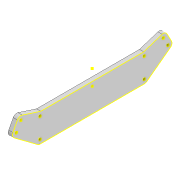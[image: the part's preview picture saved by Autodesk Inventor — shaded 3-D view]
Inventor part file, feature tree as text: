
AUTODESK INVENTOR PART (.ipt)
format: ipt  version: 2022 (Build 260153000, 153)  size: 279,040 bytes
history: native  units: mm
features: sketch x2, extrude x1, projected_geometry x1
ambient origin geometry x8: Origin, YZ Plane, XZ Plane, XY Plane, X Axis, Y Axis, Z Axis, Center Point
bodies: Solid1 (feature_tree)
feature tree (4):
  extrude  "Extrusion1"  Depth=3.9mm
  sketch  "Sketch8"  dims[d6=5.0mm d7=0.0mm d25=3.0mm d28=3.0mm d43=59.0mm d44=65.0mm d45=65.0mm d47=59.0mm d48=10.0mm d49=10.0mm d50=10.0mm d53=3.0mm d54=3.0mm d55=4.0mm d56=4.0mm d57=25.0mm d58=25.0mm d59=10.0mm d60=10.0mm d61=10.0mm d62=3.0mm d63=3.0mm d64=3.0mm d65=3.0mm d66=3.0mm d67=10.0mm d68=25.0mm d69=3.0mm d70=3.0mm d71=10.0mm d72=25.0mm d73=25.0mm d74=25.0mm d76=3.0mm d78=3.0mm d79=3.0mm d80=3.0mm d81=6.0mm d82=6.0mm d83=19.0mm d84=8.0mm d85=8.0mm d86=8.0mm d87=8.0mm d88=2.0mm d89=10.0mm d90=10.0mm d91=30.0mm d92=30.0mm]
  sketch  "Sketch1"  dims[d2=3.9mm d4=3.9mm]
  projected_geometry  "Project Cut Edges1"
